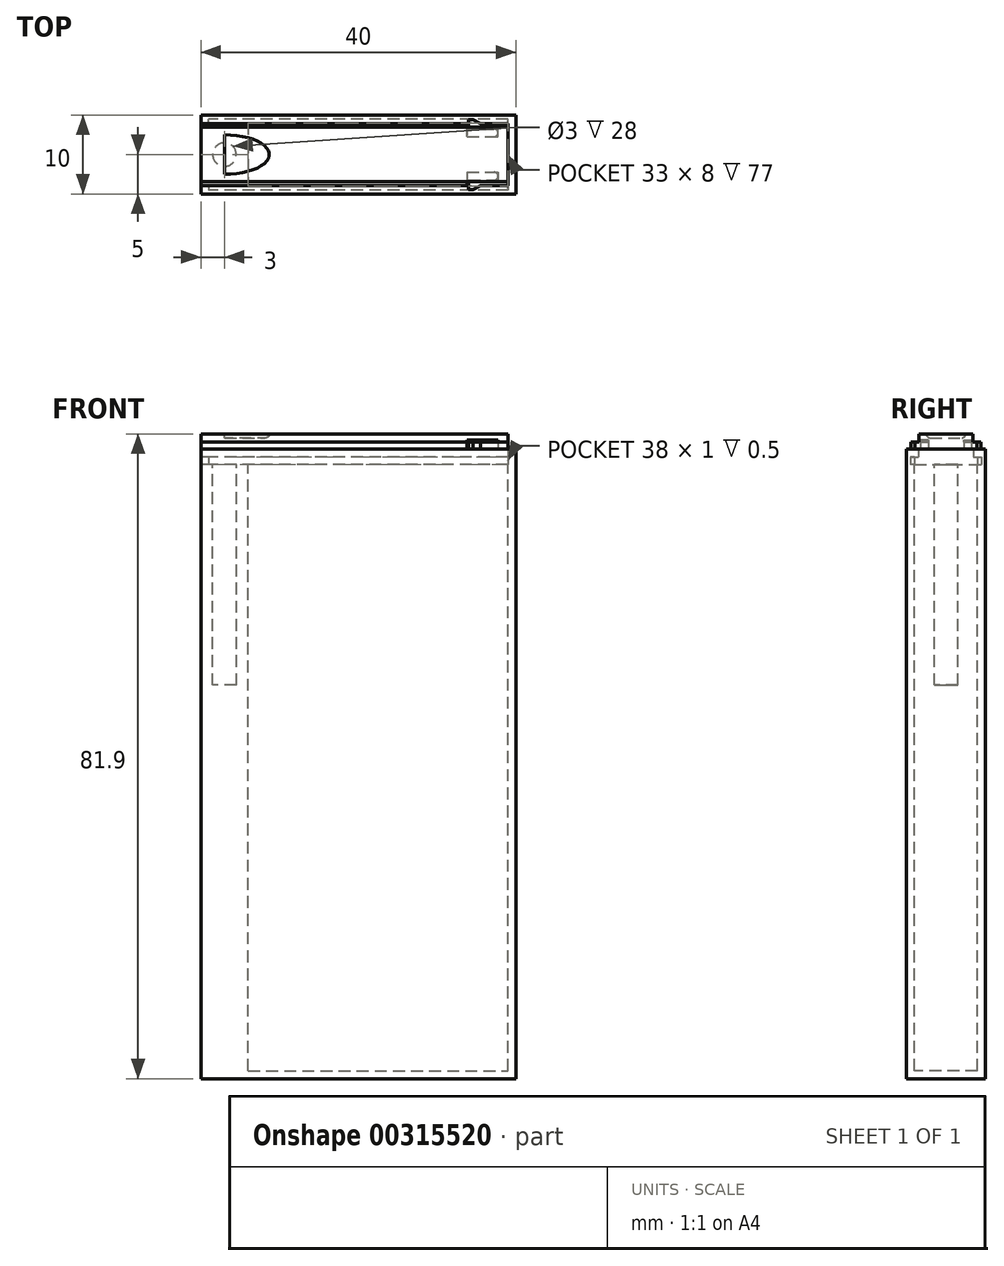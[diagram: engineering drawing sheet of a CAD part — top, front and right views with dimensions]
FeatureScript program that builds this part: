
annotation { "Feature Type Name" : "Feature", "Feature Type Description" : "" }
export const myFeature = defineFeature(function(context is Context, id is Id, definition is map)
    precondition{}
    {
        {
            var Q0;
            Q0=qCreatedBy(makeId("Top.planeOp"),FACE);
            var sketch = newSketch(context, id + "F0", { "sketchPlane" : qUnion([Q0])});
            skLineSegment(sketch, "E0.bottom", {"start": v(20, -5) * mm, "end": v(-20, -5) * mm});
            skLineSegment(sketch, "E0.top", {"start": v(20, 5) * mm, "end": v(-20, 5) * mm});
            skLineSegment(sketch, "E0.left", {"start": v(20, -5) * mm, "end": v(20, 5) * mm});
            skLineSegment(sketch, "E0.right", {"start": v(-20, -5) * mm, "end": v(-20, 5) * mm});
            skPoint(sketch, "E0.middle", {"position": v(0, 0) * mm});
            skSolve(sketch);
        }
        {
            var Q0;
            Q0 = qSketchRegion(id + "F0", true);
            extrude(context, id + "F1", {"entities" : qUnion([Q0]), "depth" : 80 * mm});
        }
        {
            var Q0;
            Q0=makeQuery(id+"F1.opExtrude","CAP_FACE",FACE,{"disambiguationData":[OSD([sQuery(id+"F0.wireOp",EDGE,"E0.bottom"),sQuery(id+"F0.wireOp",EDGE,"E0.top"),sQuery(id+"F0.wireOp",EDGE,"E0.left"),sQuery(id+"F0.wireOp",EDGE,"E0.right")])],"isStart":false});
            var sketch = newSketch(context, id + "F2", { "sketchPlane" : qUnion([Q0])});
            skLineSegment(sketch, "E1.bottom", {"start": v(-14, 4) * mm, "end": v(19, 4) * mm});
            skLineSegment(sketch, "E1.top", {"start": v(-14, -4) * mm, "end": v(19, -4) * mm});
            skLineSegment(sketch, "E1.left", {"start": v(-14, 4) * mm, "end": v(-14, -4) * mm});
            skLineSegment(sketch, "E1.right", {"start": v(19, 4) * mm, "end": v(19, -4) * mm});
            skSolve(sketch);
        }
        {
            var Q0;
            Q0 = qSketchRegion(id + "F2", true);
            extrude(context, id + "F3", {"entities" : qUnion([Q0]), "operationType" : NewBodyOperationType.REMOVE, "oppositeDirection" : true, "depth" : 79 * mm, "hasSecondDirection" : true, "secondDirectionOppositeDirection" : true, "secondDirectionDepth" : 2 * mm});
        }
        {
            var Q0;
            Q0=makeQuery(id+"F1.opExtrude","CAP_FACE",FACE,{"disambiguationData":[OSD([sQuery(id+"F0.wireOp",EDGE,"E0.bottom"),sQuery(id+"F0.wireOp",EDGE,"E0.top"),sQuery(id+"F0.wireOp",EDGE,"E0.left"),sQuery(id+"F0.wireOp",EDGE,"E0.right")])],"isStart":false});
            var sketch = newSketch(context, id + "F4", { "sketchPlane" : qUnion([Q0])});
            skCircle(sketch, "E2", {"center": v(-17, 0) * mm, "radius": 1.5 * mm});
            skSolve(sketch);
        }
        {
            var Q0;
            Q0 = qSketchRegion(id + "F4", true);
            extrude(context, id + "F5", {"entities" : qUnion([Q0]), "operationType" : NewBodyOperationType.REMOVE, "oppositeDirection" : true, "depth" : 30 * mm, "hasSecondDirection" : true, "secondDirectionOppositeDirection" : true, "secondDirectionDepth" : 2 * mm});
        }
        {
            var Q0;
            Q0=makeQuery(id+"F1.opExtrude","SWEPT_FACE",FACE,{"disambiguationData":[OSD([sQuery(id+"F0.wireOp",EDGE,"E0.right")])]});
            var sketch = newSketch(context, id + "F6", { "sketchPlane" : qUnion([Q0])});
            skLineSegment(sketch, "E3.0", {"start": v(3.5, 80) * mm, "end": v(-3.5, 80) * mm});
            skLineSegment(sketch, "E4.0", {"start": v(4, 78) * mm, "end": v(-4, 78) * mm});
            skPoint(sketch, "E5.orphan", {"position": v(-5, 0) * mm});
            skPoint(sketch, "E6.orphan", {"position": v(5, 0) * mm});
            skLineSegment(sketch, "E7.0", {"start": v(-3.5, 80) * mm, "end": v(-3.5, 79) * mm});
            skLineSegment(sketch, "E8.0", {"start": v(3.5, 80) * mm, "end": v(3.5, 79) * mm});
            skLineSegment(sketch, "E9.0", {"start": v(-4, 79) * mm, "end": v(-4, 78) * mm});
            skLineSegment(sketch, "E10.0", {"start": v(4, 79) * mm, "end": v(4, 78) * mm});
            skLineSegment(sketch, "E11.0", {"start": v(4, 79) * mm, "end": v(3.5, 79) * mm});
            skLineSegment(sketch, "E12.trimOffspring", {"start": v(-3.5, 79) * mm, "end": v(-4, 79) * mm});
            skPoint(sketch, "E13.orphan", {"position": v(5, 80) * mm});
            skPoint(sketch, "E14.0.start.orphan", {"position": v(-5, 80) * mm});
            skSolve(sketch);
        }
        {
            var Q0;
            Q0 = qSketchRegion(id + "F6", true);
            extrude(context, id + "F7", {"entities" : qUnion([Q0]), "operationType" : NewBodyOperationType.REMOVE, "oppositeDirection" : true, "depth" : 39 * mm});
        }
        {
            var Q0;
            Q0=makeQuery(id+"F1.opExtrude","SWEPT_FACE",FACE,{"disambiguationData":[OSD([sQuery(id+"F0.wireOp",EDGE,"E0.right")])]});
            var sketch = newSketch(context, id + "F8", { "sketchPlane" : qUnion([Q0])});
            skLineSegment(sketch, "E15.bottom", {"start": v(4, 79) * mm, "end": v(4.5, 79) * mm});
            skLineSegment(sketch, "E15.top", {"start": v(4, 78) * mm, "end": v(4.5, 78) * mm});
            skLineSegment(sketch, "E15.left", {"start": v(4, 79) * mm, "end": v(4, 78) * mm});
            skLineSegment(sketch, "E15.right", {"start": v(4.5, 79) * mm, "end": v(4.5, 78) * mm});
            skLineSegment(sketch, "E16.bottom", {"start": v(-4, 79) * mm, "end": v(-4.5, 79) * mm});
            skLineSegment(sketch, "E16.top", {"start": v(-4, 78) * mm, "end": v(-4.5, 78) * mm});
            skLineSegment(sketch, "E16.left", {"start": v(-4, 79) * mm, "end": v(-4, 78) * mm});
            skLineSegment(sketch, "E16.right", {"start": v(-4.5, 79) * mm, "end": v(-4.5, 78) * mm});
            skSolve(sketch);
        }
        {
            var Q0;
            Q0 = qSketchRegion(id + "F8", true);
            extrude(context, id + "F9", {"entities" : qUnion([Q0]), "operationType" : NewBodyOperationType.REMOVE, "oppositeDirection" : true, "depth" : 39 * mm, "hasSecondDirection" : true, "secondDirectionOppositeDirection" : true, "secondDirectionDepth" : 1 * mm});
        }
        {
            var Q0;
            Q0=makeQuery(id+"F1.opExtrude","CAP_FACE",FACE,{"disambiguationData":[OSD([sQuery(id+"F0.wireOp",EDGE,"E0.bottom"),sQuery(id+"F0.wireOp",EDGE,"E0.top"),sQuery(id+"F0.wireOp",EDGE,"E0.left"),sQuery(id+"F0.wireOp",EDGE,"E0.right")])],"isStart":false});
            var sketch = newSketch(context, id + "F10", { "sketchPlane" : qUnion([Q0])});
            skLineSegment(sketch, "E17.0", {"start": v(19, -3.5) * mm, "end": v(19, 3.5) * mm});
            skLineSegment(sketch, "E18.0", {"start": v(19, -3.95) * mm, "end": v(19, -3.5) * mm});
            skLineSegment(sketch, "E19.0", {"start": v(19, 3.5) * mm, "end": v(19, 3.95) * mm});
            skLineSegment(sketch, "E20.0", {"start": v(14, -4.45) * mm, "end": v(14, -3.95) * mm});
            skLineSegment(sketch, "E21", {"start": v(14.6, 4.45) * mm, "end": v(15.5, 3.95) * mm});
            skLineSegment(sketch, "E22", {"start": v(14.6, -4.45) * mm, "end": v(15.5, -3.95) * mm});
            skLineSegment(sketch, "E23", {"start": v(15.5, 3.95) * mm, "end": v(19, 3.95) * mm});
            skLineSegment(sketch, "E24", {"start": v(15.5, -3.95) * mm, "end": v(19, -3.95) * mm});
            skLineSegment(sketch, "E25.trimOffspring", {"start": v(14, 3.95) * mm, "end": v(14, 4.45) * mm});
            skLineSegment(sketch, "E26", {"start": v(14, 3.95) * mm, "end": v(14, 3.5) * mm});
            skLineSegment(sketch, "E27.0", {"start": v(13.8, 3.95) * mm, "end": v(13.8, 3.5) * mm});
            skLineSegment(sketch, "E28.trimOffspring", {"start": v(14, -3.5) * mm, "end": v(14, -3.95) * mm});
            skLineSegment(sketch, "E29.trimOffspring", {"start": v(13.8, -3.5) * mm, "end": v(13.8, -3.95) * mm});
            skLineSegment(sketch, "E30.0", {"start": v(14, 3.25) * mm, "end": v(17.25, 3.25) * mm});
            skLineSegment(sketch, "E31.0", {"start": v(14, -3.25) * mm, "end": v(17.25, -3.25) * mm});
            skLineSegment(sketch, "E32.0", {"start": v(13.8, 2.25) * mm, "end": v(17.25, 2.25) * mm});
            skLineSegment(sketch, "E33.0", {"start": v(13.8, -2.25) * mm, "end": v(17.25, -2.25) * mm});
            skPoint(sketch, "E34.startSnap0", {"position": v(17.25, -3.95) * mm});
            skArc(sketch, "E35", {"start": v(17.25, 2.25) * mm, "mid": v(17.75, 2.75) * mm, "end": v(17.25, 3.25) * mm});
            skArc(sketch, "E36", {"start": v(17.25, -3.25) * mm, "mid": v(17.75, -2.75) * mm, "end": v(17.25, -2.25) * mm});
            skLineSegment(sketch, "E37", {"start": v(13.8, 3.5) * mm, "end": v(13.8, 2.25) * mm});
            skLineSegment(sketch, "E38.trimOffspring", {"start": v(13.8, -2.25) * mm, "end": v(13.8, -3.5) * mm});
            skLineSegment(sketch, "E39", {"start": v(14, 3.5) * mm, "end": v(14, 3.25) * mm});
            skLineSegment(sketch, "E40", {"start": v(14, -3.25) * mm, "end": v(14, -3.5) * mm});
            skLineSegment(sketch, "E41.0", {"start": v(-20, -3.95) * mm, "end": v(-20, 3.95) * mm});
            skLineSegment(sketch, "E42", {"start": v(-20, -3.95) * mm, "end": v(13.8, -3.95) * mm});
            skLineSegment(sketch, "E43.0", {"start": v(-20, 3.95) * mm, "end": v(13.8, 3.95) * mm});
            skPoint(sketch, "E44.orphan", {"position": v(13.8, -3.95) * mm});
            skLineSegment(sketch, "E45.0", {"start": v(14.6, 4.45) * mm, "end": v(14, 4.45) * mm});
            skPoint(sketch, "E46.orphan", {"position": v(14.5, 4.5) * mm});
            skLineSegment(sketch, "E47.0", {"start": v(14.6, -4.45) * mm, "end": v(14, -4.45) * mm});
            skPoint(sketch, "E48.trimOffspring.start.orphan", {"position": v(14.5, -4.5) * mm});
            skSolve(sketch);
        }
        {
            var Q0;
            Q0 = qSketchRegion(id + "F10", true);
            extrude(context, id + "F11", {"entities" : qUnion([Q0]), "depth" : 0.9 * mm});
        }
        {
            var Q0;
            Q0=makeQuery(id+"F11.opExtrude","CAP_FACE",FACE,{"disambiguationData":[OSD([sQuery(id+"F10.wireOp",EDGE,"E17.0"),sQuery(id+"F10.wireOp",EDGE,"E18.0"),sQuery(id+"F10.wireOp",EDGE,"E19.0"),sQuery(id+"F10.wireOp",EDGE,"E20.0"),sQuery(id+"F10.wireOp",EDGE,"E21"),sQuery(id+"F10.wireOp",EDGE,"E22"),sQuery(id+"F10.wireOp",EDGE,"E23"),sQuery(id+"F10.wireOp",EDGE,"E24"),sQuery(id+"F10.wireOp",EDGE,"E25.trimOffspring"),sQuery(id+"F10.wireOp",EDGE,"E26"),sQuery(id+"F10.wireOp",EDGE,"E27.0"),sQuery(id+"F10.wireOp",EDGE,"E28.trimOffspring"),sQuery(id+"F10.wireOp",EDGE,"E29.trimOffspring"),sQuery(id+"F10.wireOp",EDGE,"E30.0"),sQuery(id+"F10.wireOp",EDGE,"E31.0"),sQuery(id+"F10.wireOp",EDGE,"E32.0"),sQuery(id+"F10.wireOp",EDGE,"E33.0"),sQuery(id+"F10.wireOp",EDGE,"E35"),sQuery(id+"F10.wireOp",EDGE,"E36"),sQuery(id+"F10.wireOp",EDGE,"E37"),sQuery(id+"F10.wireOp",EDGE,"E38.trimOffspring"),sQuery(id+"F10.wireOp",EDGE,"E39"),sQuery(id+"F10.wireOp",EDGE,"E40"),sQuery(id+"F10.wireOp",EDGE,"E41.0"),sQuery(id+"F10.wireOp",EDGE,"E42"),sQuery(id+"F10.wireOp",EDGE,"E43.0"),sQuery(id+"F10.wireOp",EDGE,"E45.0"),sQuery(id+"F10.wireOp",EDGE,"E47.0")])],"isStart":false});
            var sketch = newSketch(context, id + "F12", { "sketchPlane" : qUnion([Q0])});
            skLineSegment(sketch, "E49.bottom", {"start": v(-20, -3.45) * mm, "end": v(19, -3.45) * mm});
            skLineSegment(sketch, "E49.top", {"start": v(-20, 3.45) * mm, "end": v(19, 3.45) * mm});
            skLineSegment(sketch, "E49.left", {"start": v(-20, -3.45) * mm, "end": v(-20, 3.45) * mm});
            skLineSegment(sketch, "E49.right", {"start": v(19, -3.45) * mm, "end": v(19, 3.45) * mm});
            skSolve(sketch);
        }
        {
            var Q0;
            Q0 = qSketchRegion(id + "F12", true);
            extrude(context, id + "F13", {"entities" : qUnion([Q0]), "operationType" : NewBodyOperationType.ADD, "depth" : 1 * mm});
        }
        {
            var Q0;
            Q0=makeQuery(id+"F13.opExtrude","SWEPT_FACE",FACE,{"disambiguationData":[OSD([sQuery(id+"F12.wireOp",EDGE,"E49.bottom")])]});
            var sketch = newSketch(context, id + "F14", { "sketchPlane" : qUnion([Q0])});
            skPoint(sketch, "E50.0", {"position": v(13.8, 80.9) * mm});
            skLineSegment(sketch, "E51.bottom", {"start": v(13.8, 80.9) * mm, "end": v(17.75, 80.9) * mm});
            skLineSegment(sketch, "E51.top", {"start": v(13.8, 81.1) * mm, "end": v(17.75, 81.1) * mm});
            skLineSegment(sketch, "E51.left", {"start": v(13.8, 80.9) * mm, "end": v(13.8, 81.1) * mm});
            skLineSegment(sketch, "E51.right", {"start": v(17.75, 80.9) * mm, "end": v(17.75, 81.1) * mm});
            skSolve(sketch);
        }
        {
            var Q0;
            Q0 = qSketchRegion(id + "F14", true);
            extrude(context, id + "F15", {"entities" : qUnion([Q0]), "operationType" : NewBodyOperationType.REMOVE, "oppositeDirection" : true, "depth" : 1.2 * mm});
        }
        {
            var Q0;
            Q0=makeQuery(id+"F13.opExtrude","SWEPT_FACE",FACE,{"disambiguationData":[OSD([sQuery(id+"F12.wireOp",EDGE,"E49.top")])]});
            var sketch = newSketch(context, id + "F16", { "sketchPlane" : qUnion([Q0])});
            skPoint(sketch, "E52.0", {"position": v(-13.8, 80.9) * mm});
            skLineSegment(sketch, "E53.bottom", {"start": v(-13.8, 80.9) * mm, "end": v(-17.75, 80.9) * mm});
            skLineSegment(sketch, "E53.top", {"start": v(-13.8, 81.1) * mm, "end": v(-17.75, 81.1) * mm});
            skLineSegment(sketch, "E53.left", {"start": v(-13.8, 80.9) * mm, "end": v(-13.8, 81.1) * mm});
            skLineSegment(sketch, "E53.right", {"start": v(-17.75, 80.9) * mm, "end": v(-17.75, 81.1) * mm});
            skSolve(sketch);
        }
        {
            var Q0;
            Q0 = qSketchRegion(id + "F16", true);
            extrude(context, id + "F17", {"entities" : qUnion([Q0]), "operationType" : NewBodyOperationType.REMOVE, "oppositeDirection" : true, "depth" : 1.2 * mm});
        }
        {
            var Q0;
            Q0=makeQuery(id+"F13.opExtrude","CAP_FACE",FACE,{"disambiguationData":[OSD([sQuery(id+"F12.wireOp",EDGE,"E49.bottom"),sQuery(id+"F12.wireOp",EDGE,"E49.top"),sQuery(id+"F12.wireOp",EDGE,"E49.left"),sQuery(id+"F12.wireOp",EDGE,"E49.right")])],"isStart":false});
            var sketch = newSketch(context, id + "F18", { "sketchPlane" : qUnion([Q0])});
            skLineSegment(sketch, "E54", {"start": v(-17, 0) * mm, "end": v(-17, 2.5) * mm});
            skLineSegment(sketch, "E55", {"start": v(-17, 0) * mm, "end": v(-17, -2.5) * mm});
            skEllipticalArc(sketch, "E56", {});
            const initialGuessF18  = {"E56": [-0.017, 0, 0, 1, 0.0025, 0.0056931805987952945, 3.141592653589793, 6.283185307179586]};
            skSetInitialGuess(sketch, initialGuessF18);
            skSolve(sketch);
        }
        {
            var Q0;
            Q0 = qSketchRegion(id + "F18", true);
            extrude(context, id + "F19", {"entities" : qUnion([Q0]), "operationType" : NewBodyOperationType.REMOVE, "oppositeDirection" : true, "depth" : 0.5 * mm});
        }
        {
            var Q0;
            Q0=makeQuery(id+"F19.boolean.opBoolean","COPY",EDGE,{"derivedFrom":makeQuery(id+"F19.opExtrude","CAP_EDGE",EDGE,{"disambiguationData":[OSD([sQuery(id+"F18.wireOp",EDGE,"E56")])],"isStart":false})});
            fillet(context, id + "F20", {"entities" : qUnion([Q0]), "radius" : 0.5 * mm, "tangentPropagation" : true, "allowEdgeOverflow" : false});
        }
    });
